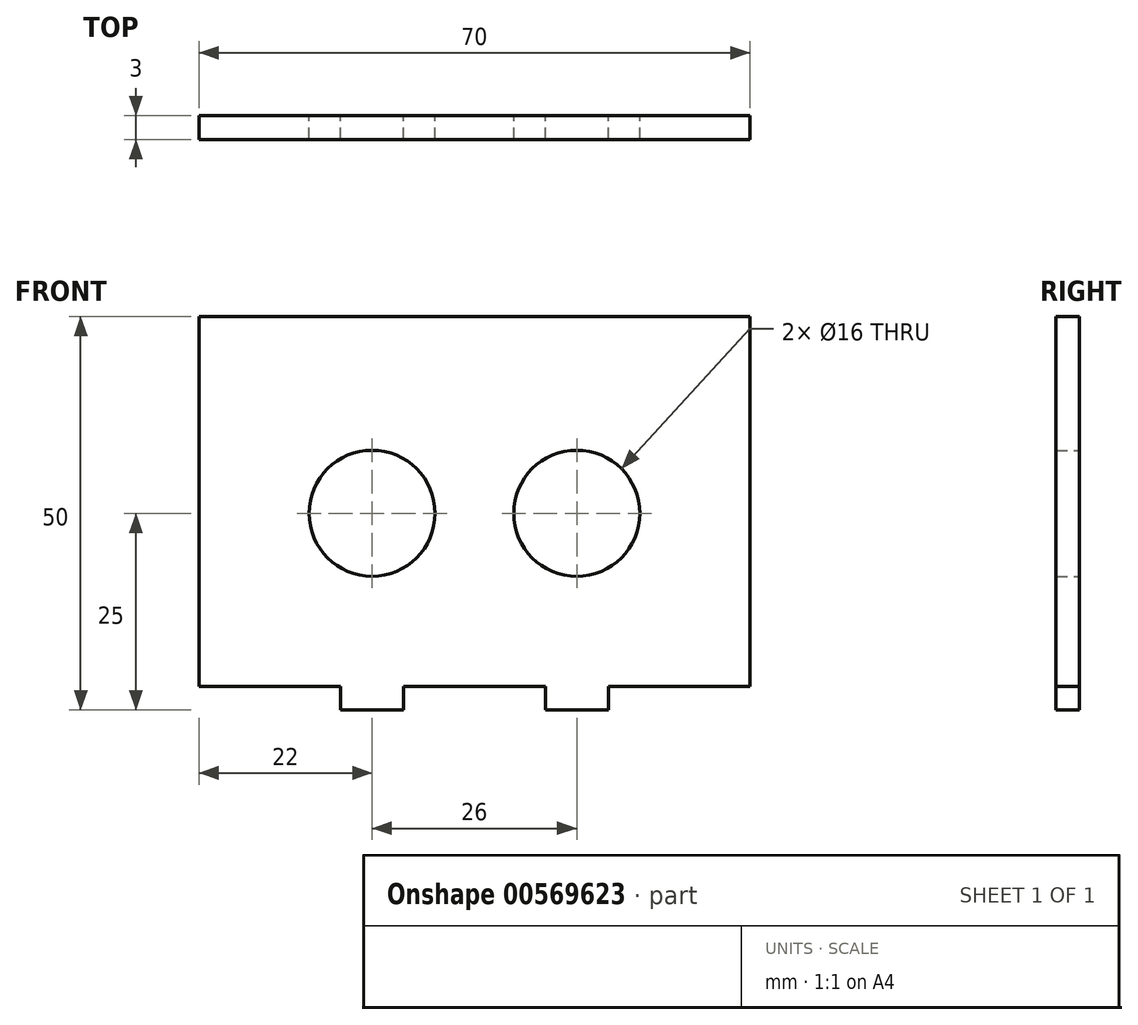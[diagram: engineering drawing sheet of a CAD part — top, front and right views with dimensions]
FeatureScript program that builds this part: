
annotation { "Feature Type Name" : "Feature", "Feature Type Description" : "" }
export const myFeature = defineFeature(function(context is Context, id is Id, definition is map)
    precondition{}
    {
        {
            var Q0;
            Q0=qCreatedBy(makeId("Front.planeOp"),FACE);
            var sketch = newSketch(context, id + "F0", { "sketchPlane" : qUnion([Q0])});
            skLineSegment(sketch, "E0.bottom", {"start": v(-35, 25) * mm, "end": v(35, 25) * mm});
            skLineSegment(sketch, "E0.top", {"start": v(-17, -25) * mm, "end": v(-9, -25) * mm});
            skLineSegment(sketch, "E0.left", {"start": v(-35, 25) * mm, "end": v(-35, -22) * mm});
            skLineSegment(sketch, "E0.right", {"start": v(35, 25) * mm, "end": v(35, -22) * mm});
            skLineSegment(sketch, "E1", {"start": v(-52.8, 0) * mm, "end": v(52.23, 0) * mm, "construction": true});
            skCircle(sketch, "E2", {"center": v(-13, 0) * mm, "radius": 8 * mm});
            skCircle(sketch, "E3", {"center": v(13, 0) * mm, "radius": 8 * mm});
            skLineSegment(sketch, "E4", {"start": v(-75.45, -22) * mm, "end": v(-73.45, -22) * mm, "construction": true});
            skLineSegment(sketch, "E5", {"start": v(-35, -22) * mm, "end": v(-17, -22) * mm});
            skLineSegment(sketch, "E6", {"start": v(-17, -22) * mm, "end": v(-17, -25) * mm});
            skLineSegment(sketch, "E7", {"start": v(-9, -25) * mm, "end": v(-9, -22) * mm});
            skPoint(sketch, "E7.endSnap0", {"position": v(-74.45, -22) * mm});
            skLineSegment(sketch, "E8", {"start": v(-9, -22) * mm, "end": v(9, -22) * mm});
            skLineSegment(sketch, "E9", {"start": v(9, -22) * mm, "end": v(9, -25) * mm});
            skLineSegment(sketch, "E10", {"start": v(9, -25) * mm, "end": v(17, -25) * mm});
            skLineSegment(sketch, "E11", {"start": v(17, -25) * mm, "end": v(17, -22) * mm});
            skLineSegment(sketch, "E12", {"start": v(17, -22) * mm, "end": v(35, -22) * mm});
            skLineSegment(sketch, "E13", {"start": v(-35, -22) * mm, "end": v(35, -22) * mm, "construction": true});
            skSolve(sketch);
        }
        {
            var Q0;
            Q0=makeQuery(id+"F0.imprint","IMPRINT",FACE,{"disambiguationData":[TD([[makeQuery(id+"F0.imprint","IMPRINT",EDGE,{"derivedFrom":sQuery(id+"F0.wireOp",EDGE,"E0.bottom")}),-1.0]])]});
            extrude(context, id + "F1", {"entities" : qUnion([Q0]), "depth" : 3 * mm, "offsetDistance" : 25 * mm});
        }
    });
